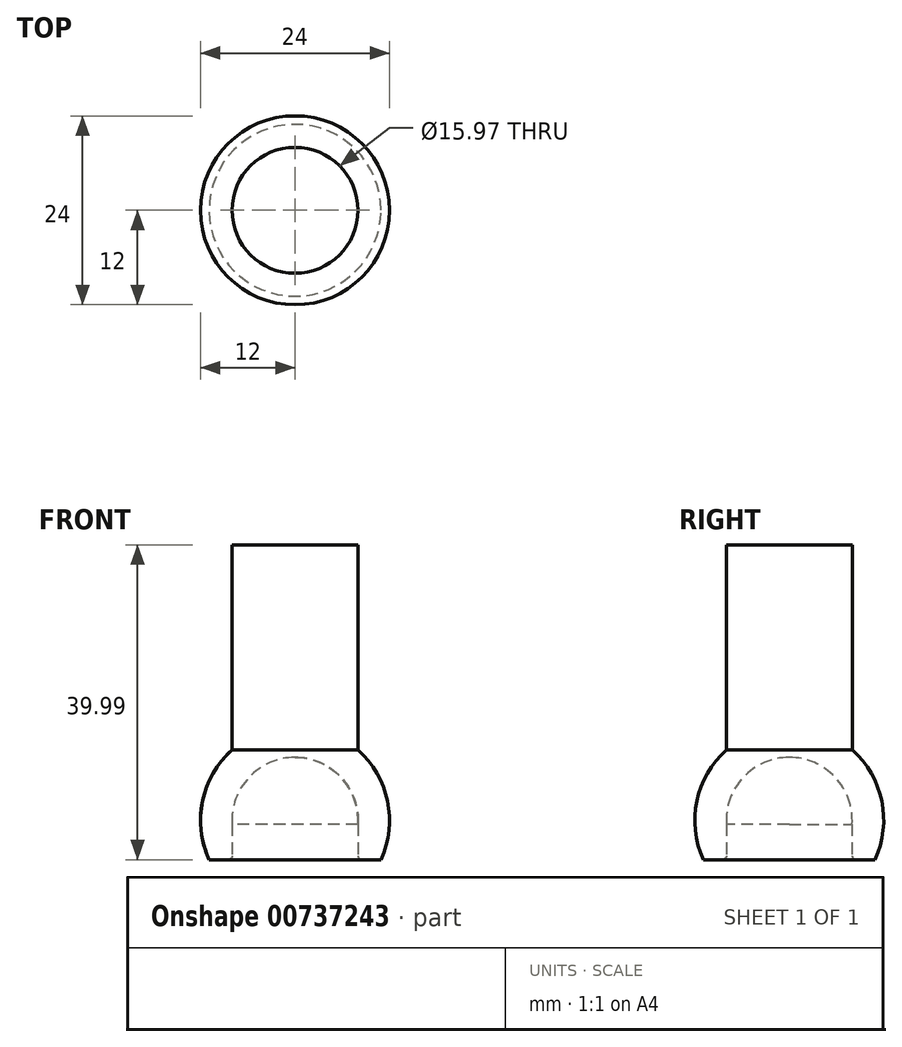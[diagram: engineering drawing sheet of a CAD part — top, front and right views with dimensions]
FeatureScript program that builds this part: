
annotation { "Feature Type Name" : "Feature", "Feature Type Description" : "" }
export const myFeature = defineFeature(function(context is Context, id is Id, definition is map)
    precondition{}
    {
        {
            var Q0;
            Q0=qCreatedBy(makeId("Front.planeOp"),FACE);
            var sketch = newSketch(context, id + "F0", { "sketchPlane" : qUnion([Q0])});
            skLineSegment(sketch, "E0", {"start": v(0, -24.76) * mm, "end": v(0, 35) * mm, "construction": true});
            skLineSegment(sketch, "E1", {"start": v(7.98, -0.5) * mm, "end": v(7.98, -5) * mm});
            skArc(sketch, "E2", {"start": v(10.91, -5) * mm, "mid": v(11.75, 2.45) * mm, "end": v(8, 8.94) * mm});
            skLineSegment(sketch, "E3", {"start": v(8, 35) * mm, "end": v(8, 8.94) * mm});
            skLineSegment(sketch, "E4", {"start": v(8, 35) * mm, "end": v(0, 35) * mm});
            skPoint(sketch, "E5.end.orphan", {"position": v(0, 8) * mm});
            skArc(sketch, "E6", {"start": v(7.98, -0.5) * mm, "mid": v(5.83, 5.48) * mm, "end": v(0, 8) * mm});
            skLineSegment(sketch, "E7", {"start": v(0, 35) * mm, "end": v(0, 8) * mm});
            skLineSegment(sketch, "E8", {"start": v(10.91, -5) * mm, "end": v(7.98, -5) * mm});
            skSolve(sketch);
        }
        {
            var Q0;
            Q0 = qSketchRegion(id + "F0", true);
            var Q1;
            Q1=sQuery(id+"F0.wireOp",EDGE,"E1");
            var Q2;
            Q2=sQuery(id+"F0.wireOp",EDGE,"E6");
            var Q3;
            Q3=sQuery(id+"F0.wireOp",EDGE,"E4");
            var Q4;
            Q4=sQuery(id+"F0.wireOp",EDGE,"E3");
            var Q5;
            Q5=sQuery(id+"F0.wireOp",EDGE,"E2");
            var Q6;
            Q6=sQuery(id+"F0.wireOp",EDGE,"CSYeR5zC-G7Gg-DDb7-Y2LW-mkgje1XfQdTl");
            var Q7;
            Q7=sQuery(id+"F0.wireOp",EDGE,"E0");
            revolve(context, id + "F1", {"surfaceOperationType" : NewSurfaceOperationType.NEW, "entities" : qUnion([Q0]), "surfaceEntities" : qUnion([Q1, Q2, Q3, Q4, Q5, Q6]), "axis" : qUnion([Q7]), "revolveType" : RevolveType.FULL});
        }
        {
            var Q0;
            Q0=makeQuery(id+"F1.opRevolve","SWEPT_EDGE",EDGE,{"disambiguationData":[OSD([sQuery(id+"F0.wireOp",EDGE,"E1"),sQuery(id+"F0.wireOp",EDGE,"E8")])]});
            fillet(context, id + "F2", {"entities" : qUnion([Q0]), "radius" : 0.5 * mm, "tangentPropagation" : true, "allowEdgeOverflow" : false});
        }
    });
